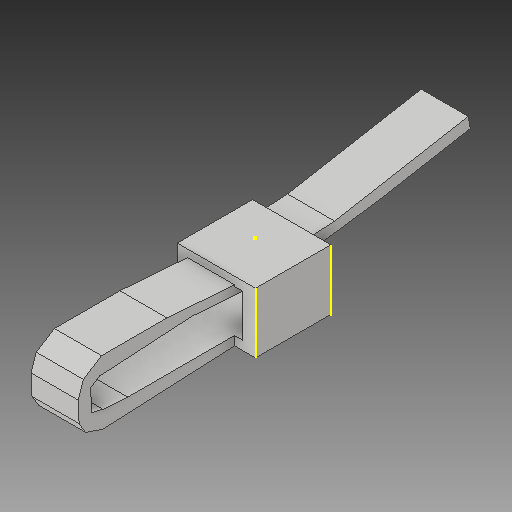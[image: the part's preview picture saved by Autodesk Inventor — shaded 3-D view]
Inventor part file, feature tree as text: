
AUTODESK INVENTOR PART (.ipt)
format: ipt  version: 2018 (Build 220112000, 112)  size: 149,504 bytes
history: native  units: mm
features: sketch x4, other x3
ambient origin geometry x8: Origin, YZ Plane, XZ Plane, XY Plane, X Axis, Y Axis, Z Axis, Center Point
bodies: Solid1 (feature_tree)
feature tree (7):
  other  "Ziptie.ipt"
  other  "Solid1::Ziptie.ipt"
  other  "TaggingFeature1"
  sketch  "Sketch1"  dims[d0=10.0mm]
  sketch  "Sketch3"
  sketch  "Sketch4"
  sketch  "Sketch5"
